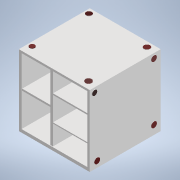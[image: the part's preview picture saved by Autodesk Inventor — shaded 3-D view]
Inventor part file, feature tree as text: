
AUTODESK INVENTOR PART (.ipt)
format: ipt  version: 2022 (Build 260153000, 153)  size: 425,984 bytes
history: native  units: mm
features: sketch x13, extrude x9, other x4
ambient origin geometry x8: Origin, YZ Plane, XZ Plane, XY Plane, X Axis, Y Axis, Z Axis, Center Point
bodies: Solid1 (feature_tree)
feature tree (26):
  sketch  "Sketch1"  dims[d0=304.8mm d1=304.8mm]
  extrude  "Extrusion1"  Depth=304.8mm
  extrude  "Extrusion2"  Depth=304.8mm
  extrude  "Extrusion3"  Depth=282.8mm
  sketch  "Sketch5"  dims[d12=300.0mm d13=0.0mm d39=2.0mm d40=0.0mm]
  sketch  "Sketch6"  dims[d41=2.0mm d42=0.0mm d43=2.0mm d44=0.0mm]
  other  "Decal1"
  other  "Decal2"
  sketch  "Sketch7"  dims[d45=2.0mm d46=0.0mm d47=2.0mm d48=0.0mm]
  extrude  "Extrusion4"  Depth=302.8mm TaperAngle=0.0deg
  extrude  "Extrusion5"  Depth=2.0mm TaperAngle=0.0deg
  extrude  "Extrusion6"  Depth=2.0mm TaperAngle=0.0deg
  extrude  "Extrusion7"  Depth=2.0mm TaperAngle=0.0deg
  sketch  "Sketch11"
  extrude  "Extrusion8"  Depth=2.0mm
  extrude  "Extrusion9"  [1 undecoded]
  sketch  "Sketch2"  dims[d2=304.8mm d3=304.8mm]
  sketch  "Sketch3"  dims[d4=304.8mm d5=0.0mm d8=282.8mm]
  sketch  "Sketch4"  dims[d9=282.8mm d10=302.8mm d11=0.0mm]
  other  "Image2"
  other  "Image3"
  sketch  "Sketch8"  dims[d49=2.0mm d50=0.0mm d14=0.5mm]
  sketch  "Sketch9"  dims[d15=0.872665mm]
  sketch  "Sketch10"
  sketch  "Sketch12"
  sketch  "Sketch13"
note: 1 required parameter value undecoded (feature->parameter linkage not recoverable at this tier; creation-order binding heuristic only, values carry confidence <= 0.55)
